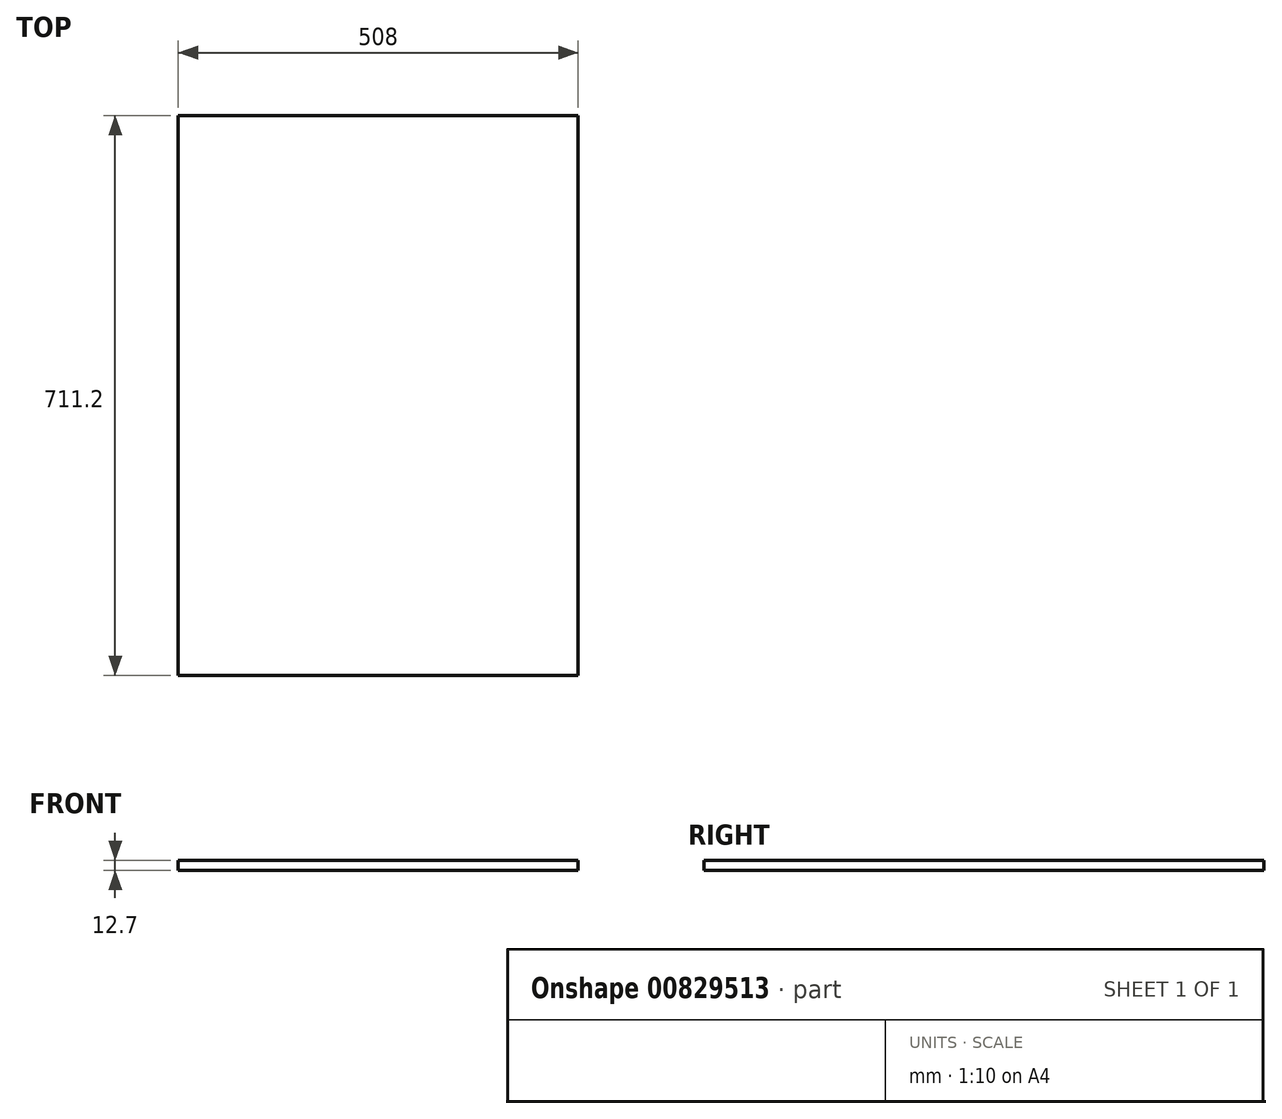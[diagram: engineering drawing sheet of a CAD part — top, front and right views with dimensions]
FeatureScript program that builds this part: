
annotation { "Feature Type Name" : "Feature", "Feature Type Description" : "" }
export const myFeature = defineFeature(function(context is Context, id is Id, definition is map)
    precondition{}
    {
        {
            var Q0;
            Q0=qCreatedBy(makeId("Top.planeOp"),FACE);
            var sketch = newSketch(context, id + "F0", { "sketchPlane" : qUnion([Q0])});
            skLineSegment(sketch, "E0.bottom", {"start": v(254, -355.6) * mm, "end": v(-254, -355.6) * mm});
            skLineSegment(sketch, "E0.top", {"start": v(254, 355.6) * mm, "end": v(-254, 355.6) * mm});
            skLineSegment(sketch, "E0.left", {"start": v(254, -355.6) * mm, "end": v(254, 355.6) * mm});
            skLineSegment(sketch, "E0.right", {"start": v(-254, -355.6) * mm, "end": v(-254, 355.6) * mm});
            skPoint(sketch, "E0.middle", {"position": v(0, 0) * mm});
            skSolve(sketch);
        }
        {
            var Q0;
            Q0 = qSketchRegion(id + "F0", true);
            extrude(context, id + "F1", {"entities" : qUnion([Q0]), "depth" : 12.7 * mm, "offsetDistance" : 25.4 * mm});
        }
    });
